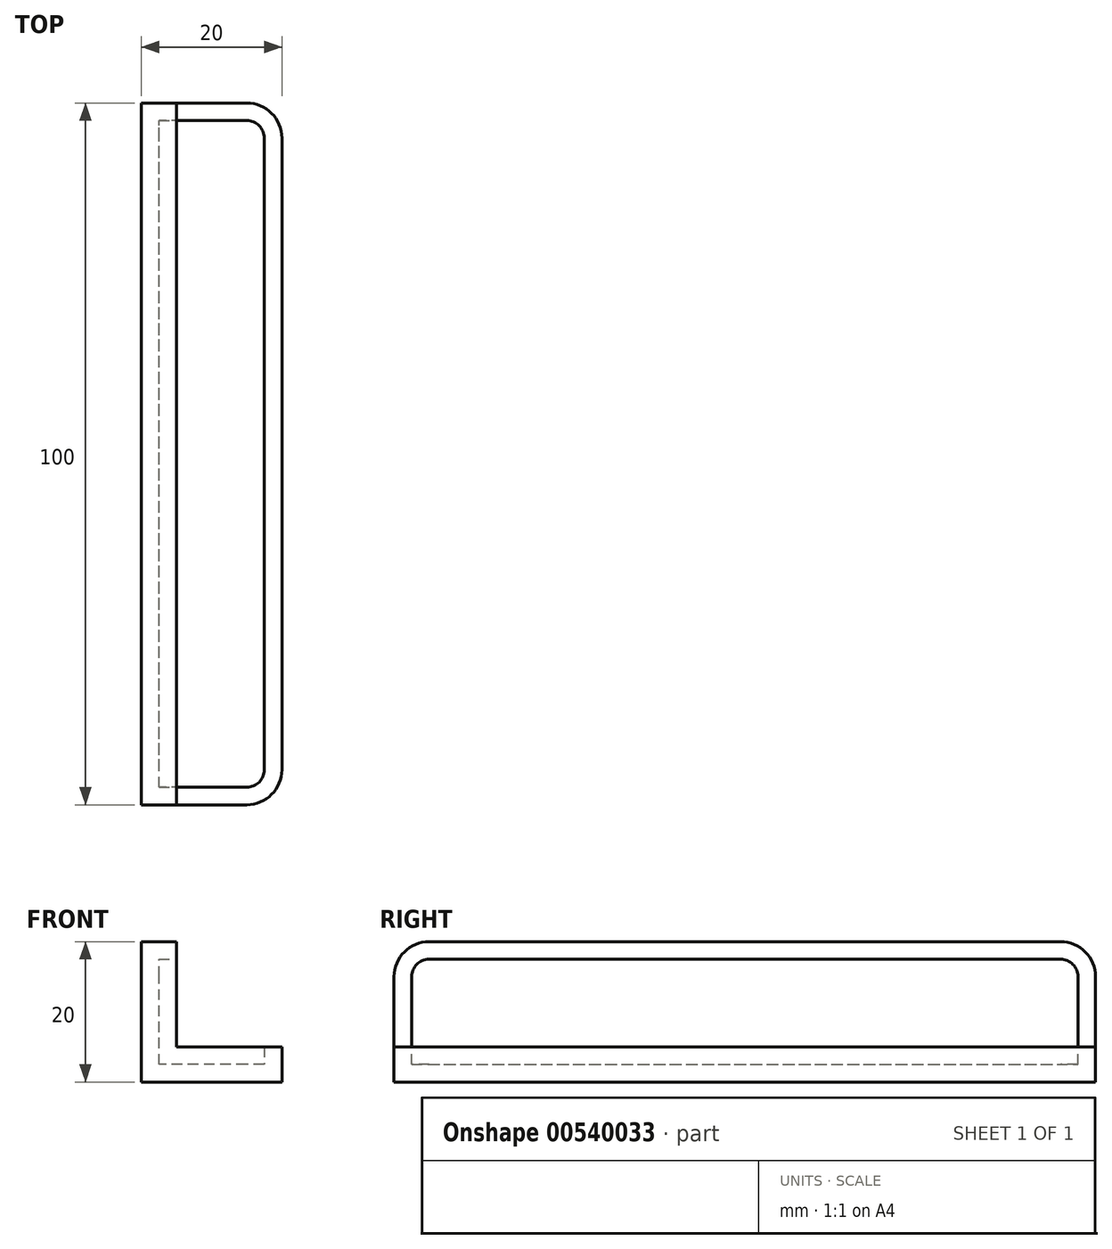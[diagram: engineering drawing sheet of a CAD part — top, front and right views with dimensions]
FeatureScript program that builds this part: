
annotation { "Feature Type Name" : "Feature", "Feature Type Description" : "" }
export const myFeature = defineFeature(function(context is Context, id is Id, definition is map)
    precondition{}
    {
        {
            var Q0;
            Q0=qCreatedBy(makeId("Front.planeOp"),FACE);
            var sketch = newSketch(context, id + "F0", { "sketchPlane" : qUnion([Q0])});
            skLineSegment(sketch, "E0", {"start": v(0, 0) * mm, "end": v(0, 20) * mm});
            skLineSegment(sketch, "E1", {"start": v(0, 20) * mm, "end": v(5, 20) * mm});
            skLineSegment(sketch, "E2", {"start": v(5, 20) * mm, "end": v(5, 5) * mm});
            skLineSegment(sketch, "E3", {"start": v(5, 5) * mm, "end": v(20, 5) * mm});
            skLineSegment(sketch, "E4", {"start": v(20, 5) * mm, "end": v(20, 0) * mm});
            skLineSegment(sketch, "E5", {"start": v(20, 0) * mm, "end": v(0, 0) * mm});
            skSolve(sketch);
        }
        {
            var Q0;
            Q0=makeQuery(id+"F0.imprint","IMPRINT",FACE,{"disambiguationData":[TD([[makeQuery(id+"F0.imprint","IMPRINT",EDGE,{"derivedFrom":sQuery(id+"F0.wireOp",EDGE,"E0")}),-1.0]])]});
            extrude(context, id + "F1", {"entities" : qUnion([Q0]), "endBound" : BoundingType.SYMMETRIC, "depth" : 100 * mm, "offsetDistance" : 25 * mm});
        }
        {
            var Q0;
            Q0=makeQuery(id+"F1.opExtrude","CAP_EDGE",EDGE,{"disambiguationData":[OSD([sQuery(id+"F0.wireOp",EDGE,"E1")])],"isStart":false});
            var Q1;
            Q1=makeQuery(id+"F1.opExtrude","CAP_EDGE",EDGE,{"disambiguationData":[OSD([sQuery(id+"F0.wireOp",EDGE,"E1")])],"isStart":true});
            var Q2;
            Q2=makeQuery(id+"F1.opExtrude","CAP_EDGE",EDGE,{"disambiguationData":[OSD([sQuery(id+"F0.wireOp",EDGE,"E4")])],"isStart":false});
            var Q3;
            Q3=makeQuery(id+"F1.opExtrude","CAP_EDGE",EDGE,{"disambiguationData":[OSD([sQuery(id+"F0.wireOp",EDGE,"E4")])],"isStart":true});
            fillet(context, id + "F2", {"entities" : qUnion([Q0, Q1, Q2, Q3]), "radius" : 5 * mm, "tangentPropagation" : true, "allowEdgeOverflow" : false});
        }
        {
            var Q0;
            Q0=makeQuery(id+"F1.opExtrude","SWEPT_FACE",FACE,{"disambiguationData":[OSD([sQuery(id+"F0.wireOp",EDGE,"E3")])]});
            var Q1;
            Q1=makeQuery(id+"F1.opExtrude","SWEPT_FACE",FACE,{"disambiguationData":[OSD([sQuery(id+"F0.wireOp",EDGE,"E2")])]});
            shell(context, id + "F3", {"entities" : qUnion([Q0, Q1]), "thickness" : 2.5 * mm});
        }
    });
